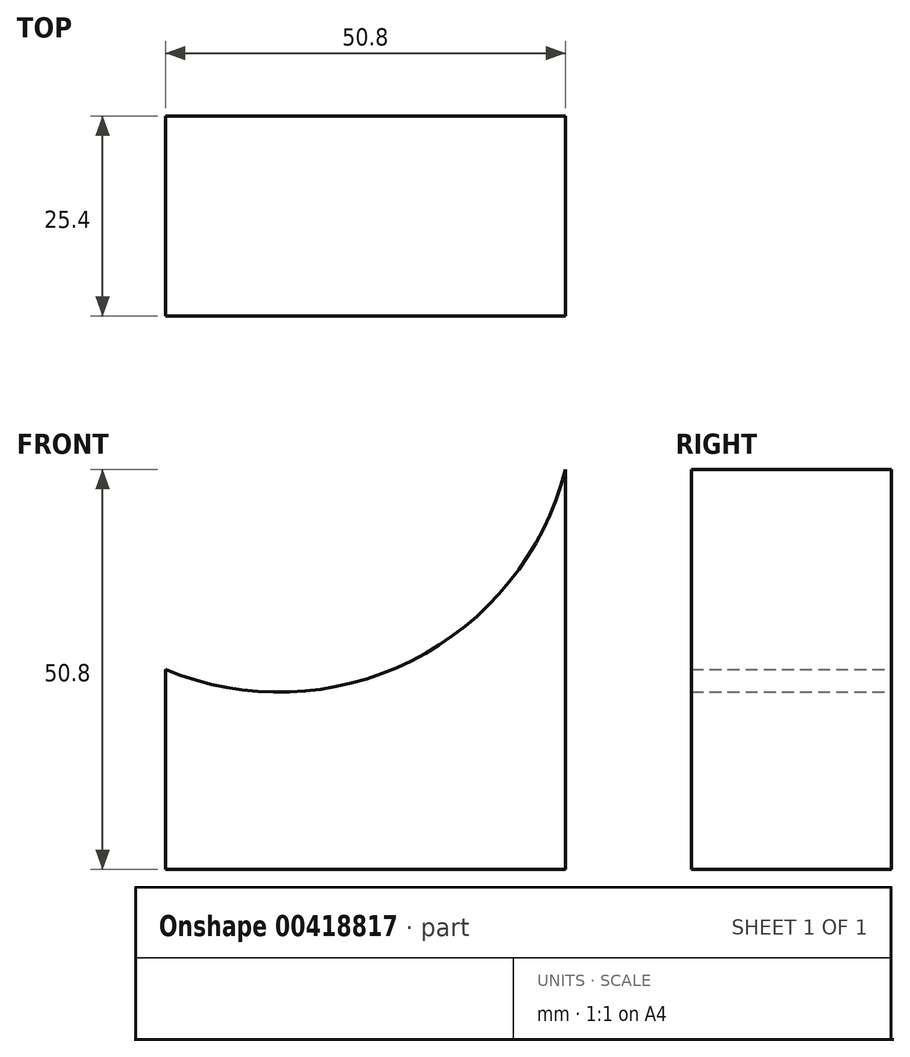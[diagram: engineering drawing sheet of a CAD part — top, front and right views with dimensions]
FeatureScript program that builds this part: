
annotation { "Feature Type Name" : "Feature", "Feature Type Description" : "" }
export const myFeature = defineFeature(function(context is Context, id is Id, definition is map)
    precondition{}
    {
        {
            var Q0;
            Q0=qCreatedBy(makeId("Front.planeOp"),FACE);
            var sketch = newSketch(context, id + "F0", { "sketchPlane" : qUnion([Q0])});
            skLineSegment(sketch, "E0", {"start": v(0, 0) * mm, "end": v(-50.8, 0) * mm});
            skLineSegment(sketch, "E1", {"start": v(-50.8, 0) * mm, "end": v(-50.8, 25.4) * mm});
            skLineSegment(sketch, "E2", {"start": v(0, 0) * mm, "end": v(0, 50.8) * mm});
            skArc(sketch, "E3", {"start": v(-50.8, 25.4) * mm, "mid": v(-19.6, 26.48) * mm, "end": v(0, 50.8) * mm});
            skSolve(sketch);
        }
        {
            var Q0;
            Q0=makeQuery(id+"F0.imprint","IMPRINT",FACE,{"disambiguationData":[TD([[makeQuery(id+"F0.imprint","IMPRINT",EDGE,{"derivedFrom":sQuery(id+"F0.wireOp",EDGE,"E0")}),-1.0]])]});
            extrude(context, id + "F1", {"entities" : qUnion([Q0]), "depth" : 25.4 * mm});
        }
    });
